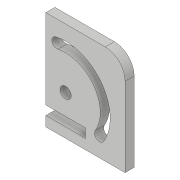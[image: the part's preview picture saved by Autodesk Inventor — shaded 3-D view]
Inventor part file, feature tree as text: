
AUTODESK INVENTOR PART (.ipt)
format: ipt  version: 2017 (Build 210142000, 142)  size: 121,856 bytes
history: native  units: in
note: dims shown in document units (in); Inventor stores cm internally (conversion verified against a paired STEP export)
features: extrude x2, fillet x2, sketch x2
ambient origin geometry x8: Origin, YZ Plane, XZ Plane, XY Plane, X Axis, Y Axis, Z Axis, Center Point
bodies: Solid1 (feature_tree)
feature tree (6):
  extrude  "Extrusion1"  Depth=1.25in
  fillet  "Fillet1"  Radius=0.25in
  extrude  "Extrusion2"  Depth=1.0in
  fillet  "Fillet2"  Radius=0.0625in
  sketch  "Sketch1"  dims[d0=0.5in d1=1.25in d2=0.25in]
  sketch  "Sketch2"  dims[d3=0.7559in d4=1.0in d5=0.0625in d6=0.0625in d7=0.115in d8=0.0in d9=0.0625in d10=1.0in d11=0.115in d12=0.5in d13=0.125in d14=0.0in d15=0.26in d16=0.0in d17=0.25in]
